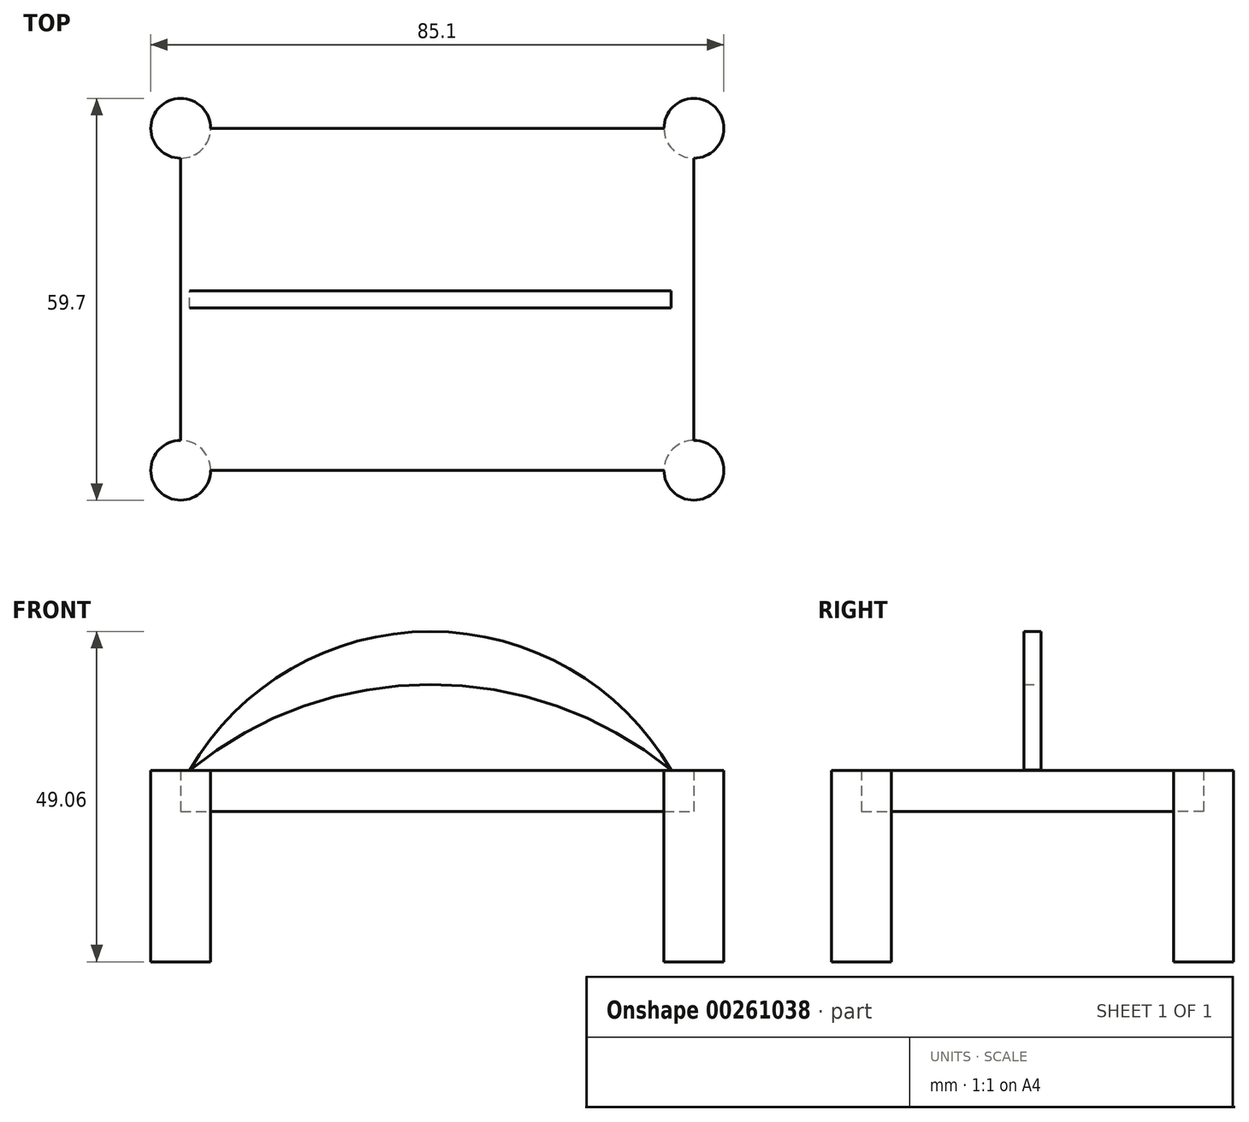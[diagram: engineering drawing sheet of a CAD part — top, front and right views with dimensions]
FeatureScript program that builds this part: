
annotation { "Feature Type Name" : "Feature", "Feature Type Description" : "" }
export const myFeature = defineFeature(function(context is Context, id is Id, definition is map)
    precondition{}
    {
        {
            var Q0;
            Q0=qCreatedBy(makeId("Top.planeOp"),FACE);
            var sketch = newSketch(context, id + "F0", { "sketchPlane" : qUnion([Q0])});
            skLineSegment(sketch, "E0.bottom", {"start": v(-38.1, 25.4) * mm, "end": v(38.1, 25.4) * mm});
            skLineSegment(sketch, "E0.top", {"start": v(-38.1, -25.4) * mm, "end": v(38.1, -25.4) * mm});
            skLineSegment(sketch, "E0.left", {"start": v(-38.1, 25.4) * mm, "end": v(-38.1, -25.4) * mm});
            skLineSegment(sketch, "E0.right", {"start": v(38.1, 25.4) * mm, "end": v(38.1, -25.4) * mm});
            skPoint(sketch, "E0.middle", {"position": v(0, 0) * mm});
            skCircle(sketch, "E1", {"center": v(-38.1, 25.4) * mm, "radius": 4.45 * mm});
            skCircle(sketch, "E2", {"center": v(38.1, 25.4) * mm, "radius": 4.45 * mm});
            skCircle(sketch, "E3", {"center": v(38.1, -25.4) * mm, "radius": 4.45 * mm});
            skCircle(sketch, "E4", {"center": v(-38.1, -25.4) * mm, "radius": 4.45 * mm});
            skSolve(sketch);
        }
        {
            var Q0;
            Q0 = qSketchRegion(id + "F0", true);
            extrude(context, id + "F1", {"entities" : qUnion([Q0]), "endBound" : BoundingType.SYMMETRIC, "depth" : 6.1 * mm});
        }
        {
            var Q0;
            Q0=qCreatedBy(makeId("Front.planeOp"),FACE);
            var sketch = newSketch(context, id + "F2", { "sketchPlane" : qUnion([Q0])});
            skArc(sketch, "E5", {"start": v(34.74, 3.07) * mm, "mid": v(-1.04, 23.66) * mm, "end": v(-36.8, 3.04) * mm});
            skArc(sketch, "E6", {"start": v(34.74, 3.07) * mm, "mid": v(-1.04, 15.79) * mm, "end": v(-36.8, 3.04) * mm});
            skSolve(sketch);
        }
        {
            var Q0;
            Q0 = qSketchRegion(id + "F2", true);
            extrude(context, id + "F3", {"entities" : qUnion([Q0]), "endBound" : BoundingType.SYMMETRIC, "depth" : 2.54 * mm});
        }
        {
            var Q0;
            {var subQ0=sQuery(id+"F0.wireOp",EDGE,"E0.left");var subQ1=sQuery(id+"F0.wireOp",EDGE,"E0.top");var subQ2=makeQuery(id+"F0.imprint","INTERSECT",VERTEX,{"derivedFrom":[subQ1,subQ0]});Q0=makeQuery(id+"F0.imprint","IMPRINT",FACE,{"disambiguationData":[TD([[makeQuery(id+"F0.imprint","IMPRINT",EDGE,{"disambiguationData":[TD([[subQ2,-1.0]])],"derivedFrom":subQ1}),-1.0]])]});}
            var Q1;
            {var subQ0=sQuery(id+"F0.wireOp",EDGE,"E0.left");var subQ1=sQuery(id+"F0.wireOp",EDGE,"E0.top");var subQ2=makeQuery(id+"F0.imprint","INTERSECT",VERTEX,{"derivedFrom":[subQ1,subQ0]});Q1=makeQuery(id+"F0.imprint","IMPRINT",FACE,{"disambiguationData":[TD([[makeQuery(id+"F0.imprint","IMPRINT",EDGE,{"disambiguationData":[TD([[subQ2,-1.0]])],"derivedFrom":subQ1}),1.0]])]});}
            var Q2;
            {var subQ0=sQuery(id+"F0.wireOp",EDGE,"E0.right");var subQ1=sQuery(id+"F0.wireOp",EDGE,"E0.top");var subQ2=makeQuery(id+"F0.imprint","INTERSECT",VERTEX,{"derivedFrom":[subQ1,subQ0]});Q2=makeQuery(id+"F0.imprint","IMPRINT",FACE,{"disambiguationData":[TD([[makeQuery(id+"F0.imprint","IMPRINT",EDGE,{"disambiguationData":[TD([[subQ2,1.0]])],"derivedFrom":subQ1}),-1.0]])]});}
            var Q3;
            {var subQ0=sQuery(id+"F0.wireOp",EDGE,"E0.right");var subQ1=sQuery(id+"F0.wireOp",EDGE,"E0.top");var subQ2=makeQuery(id+"F0.imprint","INTERSECT",VERTEX,{"derivedFrom":[subQ1,subQ0]});Q3=makeQuery(id+"F0.imprint","IMPRINT",FACE,{"disambiguationData":[TD([[makeQuery(id+"F0.imprint","IMPRINT",EDGE,{"disambiguationData":[TD([[subQ2,1.0]])],"derivedFrom":subQ1}),1.0]])]});}
            var Q4;
            {var subQ0=sQuery(id+"F0.wireOp",EDGE,"E0.right");var subQ1=sQuery(id+"F0.wireOp",EDGE,"E0.bottom");var subQ2=makeQuery(id+"F0.imprint","INTERSECT",VERTEX,{"derivedFrom":[subQ1,subQ0]});Q4=makeQuery(id+"F0.imprint","IMPRINT",FACE,{"disambiguationData":[TD([[makeQuery(id+"F0.imprint","IMPRINT",EDGE,{"disambiguationData":[TD([[subQ2,1.0]])],"derivedFrom":subQ1}),1.0]])]});}
            var Q5;
            {var subQ0=sQuery(id+"F0.wireOp",EDGE,"E0.right");var subQ1=sQuery(id+"F0.wireOp",EDGE,"E0.bottom");var subQ2=makeQuery(id+"F0.imprint","INTERSECT",VERTEX,{"derivedFrom":[subQ1,subQ0]});Q5=makeQuery(id+"F0.imprint","IMPRINT",FACE,{"disambiguationData":[TD([[makeQuery(id+"F0.imprint","IMPRINT",EDGE,{"disambiguationData":[TD([[subQ2,1.0]])],"derivedFrom":subQ1}),-1.0]])]});}
            var Q6;
            {var subQ0=sQuery(id+"F0.wireOp",EDGE,"E0.left");var subQ1=sQuery(id+"F0.wireOp",EDGE,"E0.bottom");var subQ2=makeQuery(id+"F0.imprint","INTERSECT",VERTEX,{"derivedFrom":[subQ1,subQ0]});Q6=makeQuery(id+"F0.imprint","IMPRINT",FACE,{"disambiguationData":[TD([[makeQuery(id+"F0.imprint","IMPRINT",EDGE,{"disambiguationData":[TD([[subQ2,-1.0]])],"derivedFrom":subQ1}),1.0]])]});}
            var Q7;
            {var subQ0=sQuery(id+"F0.wireOp",EDGE,"E0.left");var subQ1=sQuery(id+"F0.wireOp",EDGE,"E0.bottom");var subQ2=makeQuery(id+"F0.imprint","INTERSECT",VERTEX,{"derivedFrom":[subQ1,subQ0]});Q7=makeQuery(id+"F0.imprint","IMPRINT",FACE,{"disambiguationData":[TD([[makeQuery(id+"F0.imprint","IMPRINT",EDGE,{"disambiguationData":[TD([[subQ2,-1.0]])],"derivedFrom":subQ1}),-1.0]])]});}
            extrude(context, id + "F4", {"entities" : qUnion([Q0, Q1, Q2, Q3, Q4, Q5, Q6, Q7]), "operationType" : NewBodyOperationType.ADD, "oppositeDirection" : true, "depth" : 25.4 * mm});
        }
    });
